# Revit family: Chair-Soft_Seating-Allermuir-Pause-PSB154L-Low
name_source: partatom
category: Furniture
revit_build: Autodesk Revit MEP 2012 (Build: 20110309_2315)
units: mm (PartAtom-declared; Revit-internal decimal feet)

## types (1)
- PSB154L
    04 CSI = 12 51 00
    95 CSI = 12510
    Assembly Code = E2020200
    Brochure URL = http://www.allermuir.net
    CAD Blocks URL = http://www.allermuir.net
    Color Availability = See price list for material options
    Fabric Spec Sheets = http://www.allermuir.net
    LEED Stats URL = http://www.allermuir.net
    Leg Base = Plastic - Allermuir - Black
    Manufacturer = Allermuir
    Manufacturer Fax = (419) 887 5805
    Model = PSB154L
    Overall Depth = 1' - 4 17/32"
    Overall Height = 1' - 11 7/16"
    Overall Width = 4' - 10 31/32"
    Plugin Data URL = http://products.ecoscorecard.com
    Pricing URL = http://www.allermuir.net
    Product Line = Pause
    Product Page URL = http://www.allermuir.net
    Seat = Fabric - Allermuir - Silcoates
    Specifications URL = http://www.allermuir.net
    Stacks = No
    Stand = Metal - Allermuir - Silver
    Subcategory = Soft Seating
    URL = http://www.allermuir.net
    Upholstered Back = No
    Upholstered Seat = No
    Weight = 15.0 lb
    ecoScorecard Product Page = http://products.ecoscorecard.com
    ecoScorecard_data = http://thesenatorgroup.ecoscorecard.com

## geometry (parser evidence)
native form markers: Blend x7, Sweep x3
no freeform markers — native parametric forms only
